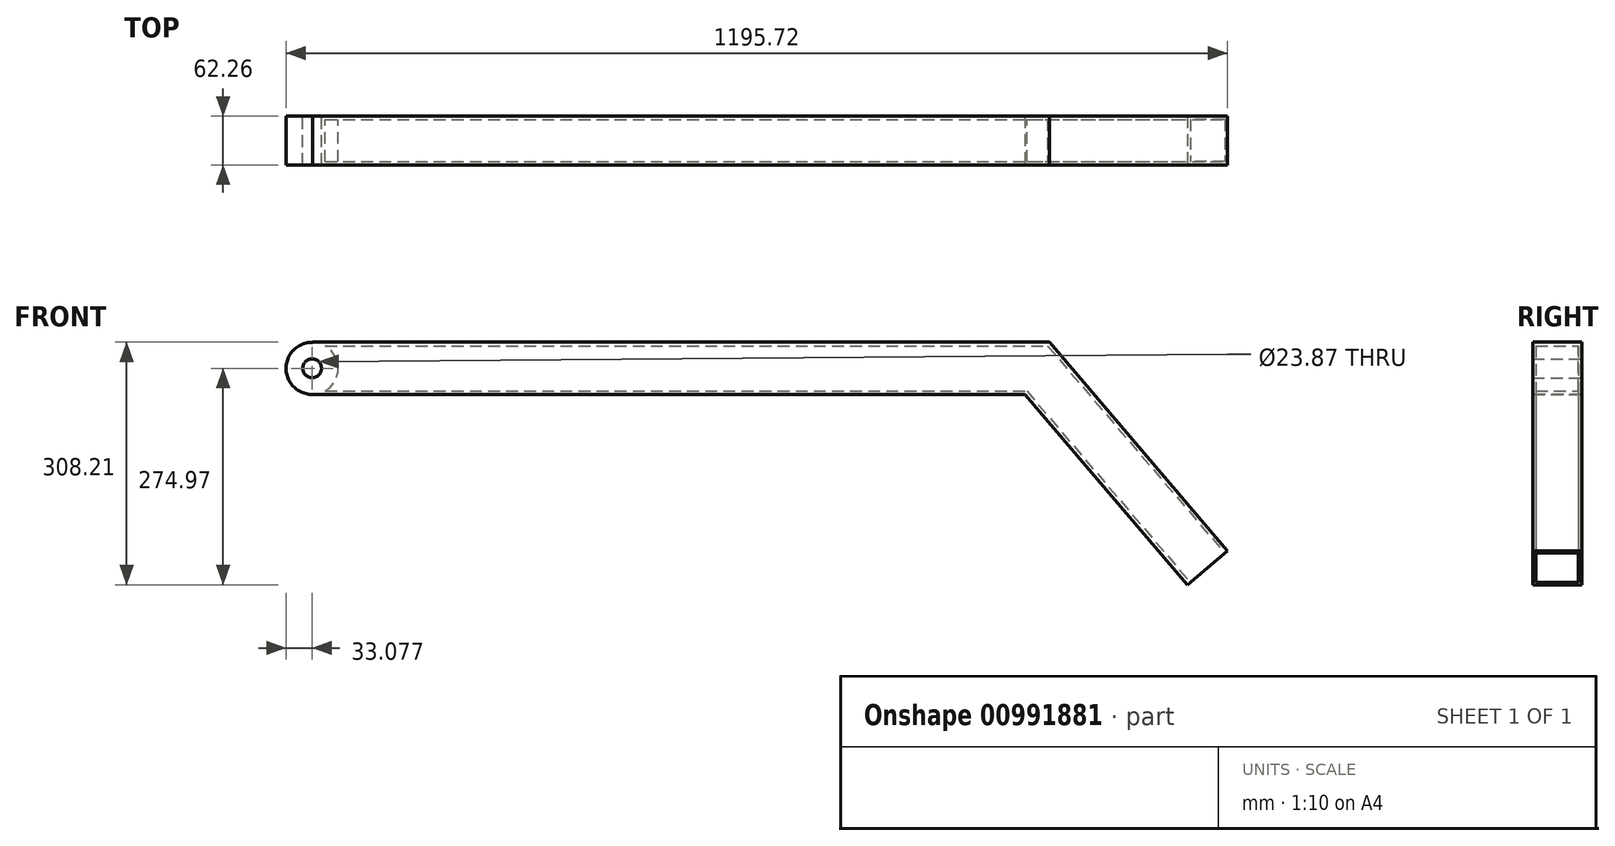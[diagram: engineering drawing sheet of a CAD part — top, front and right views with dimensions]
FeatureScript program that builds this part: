
annotation { "Feature Type Name" : "Feature", "Feature Type Description" : "" }
export const myFeature = defineFeature(function(context is Context, id is Id, definition is map)
    precondition{}
    {
        {
            var Q0;
            Q0=qCreatedBy(makeId("Front.planeOp"),FACE);
            var sketch = newSketch(context, id + "F0", { "sketchPlane" : qUnion([Q0])});
            skLineSegment(sketch, "E0", {"start": v(-920.05, 0) * mm, "end": v(0, 0) * mm});
            skLineSegment(sketch, "E1", {"start": v(0, 0) * mm, "end": v(216.42, -253.38) * mm});
            skSolve(sketch);
        }
        {
            var Q0;
            Q0=sQuery(id+"F0.wireOp",VERTEX,"E0.start");
            var Q1;
            Q1=qCreatedBy(makeId("Right.planeOp"),FACE);
            cPlane(context, id + "F1", {"entities" : qUnion([Q0, Q1]), "cplaneType" : CPlaneType.PLANE_POINT, "offset" : 25.4 * mm, "width" : 152.4 * mm, "height" : 152.4 * mm});
        }
        {
            var Q0;
            Q0=qCreatedBy(id+"F1.planeOp",FACE);
            var sketch = newSketch(context, id + "F2", { "sketchPlane" : qUnion([Q0])});
            skLineSegment(sketch, "E2.bottom", {"start": v(31.13, 33.24) * mm, "end": v(-31.13, 33.24) * mm});
            skLineSegment(sketch, "E2.top", {"start": v(31.13, -33.24) * mm, "end": v(-31.13, -33.24) * mm});
            skLineSegment(sketch, "E2.left", {"start": v(31.13, 33.24) * mm, "end": v(31.13, -33.24) * mm});
            skLineSegment(sketch, "E2.right", {"start": v(-31.13, 33.24) * mm, "end": v(-31.13, -33.24) * mm});
            skPoint(sketch, "E2.middle", {"position": v(0, 0) * mm});
            skLineSegment(sketch, "E3.bottom", {"start": v(26.92, 28.73) * mm, "end": v(-26.92, 28.73) * mm});
            skLineSegment(sketch, "E3.top", {"start": v(26.92, -28.73) * mm, "end": v(-26.92, -28.73) * mm});
            skLineSegment(sketch, "E3.left", {"start": v(26.92, 28.73) * mm, "end": v(26.92, -28.73) * mm});
            skLineSegment(sketch, "E3.right", {"start": v(-26.92, 28.73) * mm, "end": v(-26.92, -28.73) * mm});
            skSolve(sketch);
        }
        {
            var Q0;
            Q0=makeQuery(id+"F2.imprint","IMPRINT",FACE,{"disambiguationData":[TD([[makeQuery(id+"F2.imprint","IMPRINT",EDGE,{"derivedFrom":sQuery(id+"F2.wireOp",EDGE,"E2.bottom")}),1.0]])]});
            var Q1;
            Q1=sQuery(id+"F0.wireOp",EDGE,"E0");
            var Q2;
            Q2=sQuery(id+"F0.wireOp",EDGE,"E1");
            sweep(context, id + "F3", {"profiles" : qUnion([Q0]), "path" : qUnion([Q1, Q2])});
        }
        {
            var Q0;
            Q0=qCreatedBy(makeId("Front.planeOp"),FACE);
            var sketch = newSketch(context, id + "F4", { "sketchPlane" : qUnion([Q0])});
            skCircle(sketch, "E4", {"center": v(-920.95, 0) * mm, "radius": 33.08 * mm});
            skSolve(sketch);
        }
        {
            var Q0;
            Q0=makeQuery(id+"F4.imprint","IMPRINT",FACE,{"disambiguationData":[TD([[makeQuery(id+"F4.imprint","IMPRINT",EDGE,{"derivedFrom":sQuery(id+"F4.wireOp",EDGE,"E4")}),1.0]])]});
            var Q1;
            Q1=makeQuery(id+"F3.opSweep","SWEPT_FACE",FACE,{"disambiguationData":[OSD([sQuery(id+"F0.wireOp",EDGE,"E0"),sQuery(id+"F2.wireOp",EDGE,"E2.right")])]});
            var Q2;
            Q2=makeQuery(id+"F3.opSweep","SWEPT_FACE",FACE,{"disambiguationData":[OSD([sQuery(id+"F0.wireOp",EDGE,"E0"),sQuery(id+"F2.wireOp",EDGE,"E2.left")])]});
            extrude(context, id + "F5", {"entities" : qUnion([Q0]), "operationType" : NewBodyOperationType.ADD, "endBound" : BoundingType.UP_TO_SURFACE, "depth" : 69.6 * mm, "endBoundEntityFace" : qUnion([Q1]), "offsetDistance" : 25.4 * mm, "hasSecondDirection" : true, "secondDirectionBound" : SecondDirectionBoundingType.UP_TO_SURFACE, "secondDirectionOppositeDirection" : true, "secondDirectionDepth" : 25.4 * mm, "secondDirectionBoundEntityFace" : qUnion([Q2])});
        }
        {
            var Q0;
            Q0=makeQuery(id+"F5.boolean.opBoolean","MERGE",FACE,{"derivedFrom":[makeQuery(id+"F3.opSweep","SWEPT_FACE",FACE,{"disambiguationData":[OSD([sQuery(id+"F0.wireOp",EDGE,"E0"),sQuery(id+"F2.wireOp",EDGE,"E2.left")])]}),makeQuery(id+"F5.opExtrude","CAP_FACE",FACE,{"disambiguationData":[OSD([sQuery(id+"F4.wireOp",EDGE,"E4")])],"isStart":true})]});
            var sketch = newSketch(context, id + "F6", { "sketchPlane" : qUnion([Q0])});
            skCircle(sketch, "E5", {"center": v(920.95, 0) * mm, "radius": 11.94 * mm});
            skSolve(sketch);
        }
        {
            var Q0;
            Q0=makeQuery(id+"F6.imprint","IMPRINT",FACE,{"disambiguationData":[TD([[makeQuery(id+"F6.imprint","IMPRINT",EDGE,{"derivedFrom":sQuery(id+"F6.wireOp",EDGE,"E5")}),1.0]])]});
            extrude(context, id + "F7", {"entities" : qUnion([Q0]), "operationType" : NewBodyOperationType.REMOVE, "endBound" : BoundingType.UP_TO_NEXT, "oppositeDirection" : true, "depth" : 25.4 * mm, "offsetDistance" : 25.4 * mm});
        }
    });
